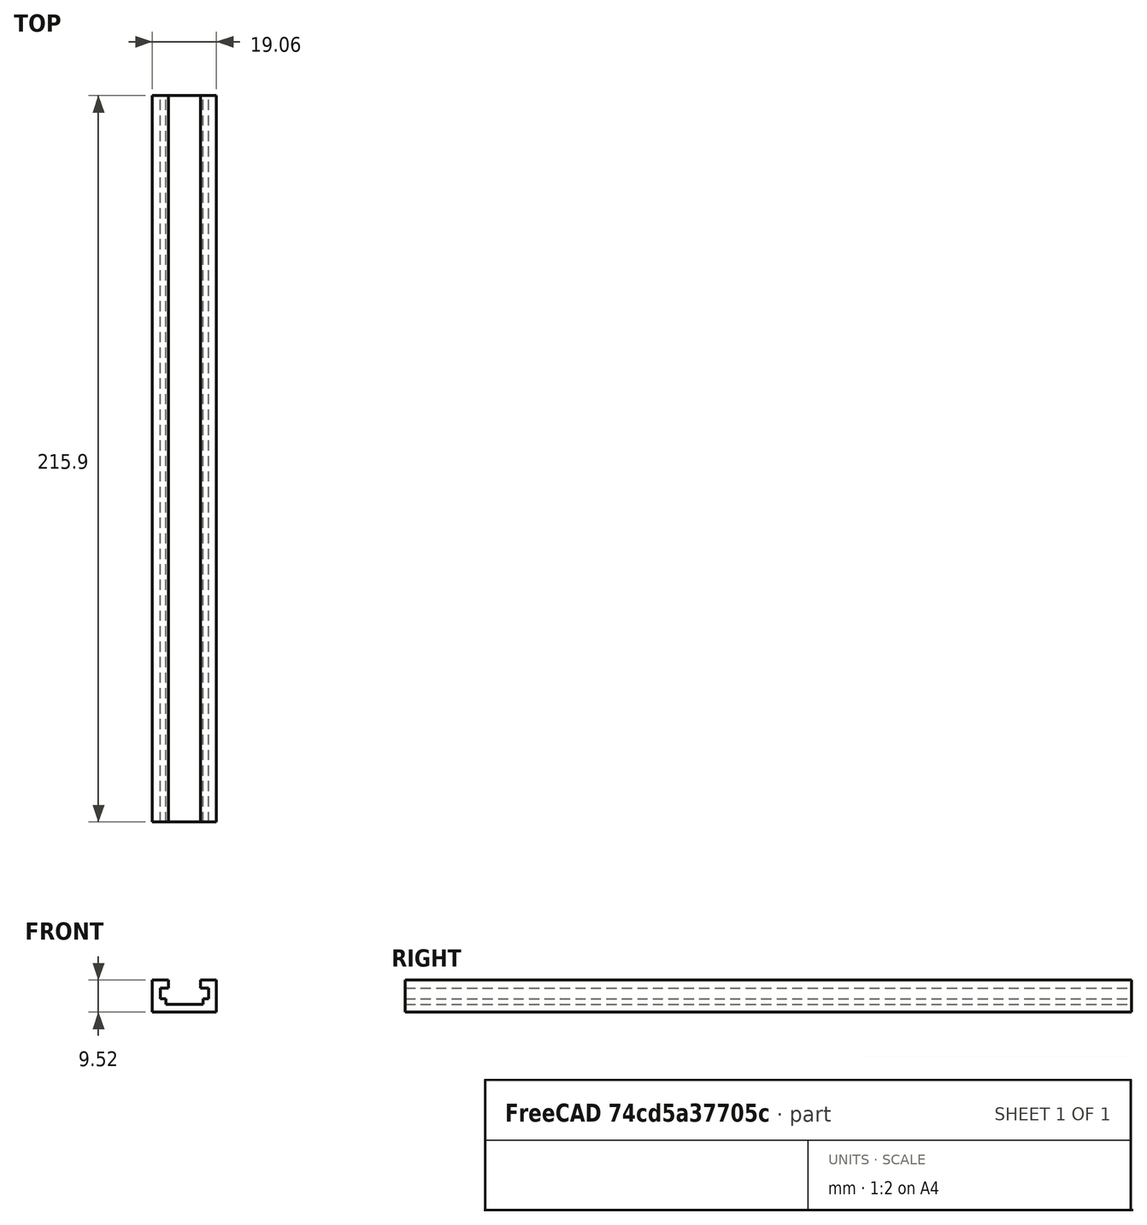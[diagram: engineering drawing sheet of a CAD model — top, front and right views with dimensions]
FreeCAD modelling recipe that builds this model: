
FCSTD DOCUMENT  (FreeCAD 0.20R29603 (Git))
Label: far_fence_top_t_track
License: All rights reserved
LicenseURL: http://en.wikipedia.org/wiki/All_rights_reserved
objects: Sketcher::SketchObject×4, PartDesign::Pocket×3, TechDraw::DrawProjGroupItem×2, PartDesign::Pad×1, PartDesign::Body×1, TechDraw::DrawSVGTemplate×1, TechDraw::DrawProjGroup×1, TechDraw::DrawViewDimension×1, TechDraw::DrawPage×1
note: 13 computed .brp shape members not serialized (recipe doc carries the construction recipe); baked Part::Feature solids carry a one-line shape summary decoded from their .brp

FEATURE [Sketcher::SketchObject] Sketch
  FullyConstrained = true
  MapMode = 5
  Placement = pos=(0,0,0) rot=(1,0,0;1.5708rad)
  Support = -> [XZ_Plane]
  sketch-geometry (5):
    g0: LineSegment StartX=-9.525 StartY=-4.7625 StartZ=0 EndX=-9.525 EndY=4.7625 EndZ=0
    g1: LineSegment StartX=-9.525 StartY=4.7625 StartZ=0 EndX=9.525 EndY=4.7625 EndZ=0
    g2: LineSegment StartX=9.525 StartY=4.7625 StartZ=0 EndX=9.525 EndY=-4.7625 EndZ=0
    g3: LineSegment StartX=9.525 StartY=-4.7625 StartZ=0 EndX=-9.525 EndY=-4.7625 EndZ=0
    g4: GeomPoint X=0 Y=0 Z=0
  constraints (12):
    c: Coincident(g0,g1)
    c: Coincident(g1,g2)
    c: Coincident(g2,g3)
    c: Coincident(g3,g0)
    c: Horizontal(g1)
    c: Horizontal(g3)
    c: Vertical(g0)
    c: Vertical(g2)
    c: Symmetric(g1,g0,g4)
    c: DistanceX(g1,g1) = 19.05
    c: DistanceY(g2,g2) = 9.525
    c: Coincident(g-1,g4)
FEATURE [PartDesign::Pad] Pad
  Direction = (0,-1,-2e-16)
  Length = 215.9
  Length2 = 10
  Placement = pos=(0,0,0) rot=(1,0,0;1.5708rad)
  Profile = -> Sketch
  ReferenceAxis = -> Sketch [N_Axis]
  Type = 0
FEATURE [Sketcher::SketchObject] Sketch001
  ExternalGeometry = -> [Pad]
  FullyConstrained = true
  MapMode = 5
  Placement = pos=(0,-215.9,-4.75e-14) rot=(1,0,0;1.5708rad)
  Support = -> [Pad]
  sketch-geometry (5):
    g0: LineSegment StartX=-4.7625 StartY=2.38125 StartZ=0 EndX=-4.7625 EndY=4.7625 EndZ=0
    g1: LineSegment StartX=-4.7625 StartY=4.7625 StartZ=0 EndX=4.7625 EndY=4.7625 EndZ=0
    g2: LineSegment StartX=4.7625 StartY=4.7625 StartZ=0 EndX=4.7625 EndY=2.38125 EndZ=0
    g3: LineSegment StartX=4.7625 StartY=2.38125 StartZ=0 EndX=-4.7625 EndY=2.38125 EndZ=0
    g4: GeomPoint X=0 Y=3.57187 Z=0
  constraints (12):
    c: Coincident(g0,g1)
    c: Coincident(g1,g2)
    c: Coincident(g2,g3)
    c: Coincident(g3,g0)
    c: Horizontal(g3)
    c: Vertical(g0)
    c: Vertical(g2)
    c: Symmetric(g1,g0,g4)
    c: Tangent(g1,g-3)
    c: DistanceX(g3,g3) = 9.525
    c: Distance(g2,g-4) = 7.14375
    c: PointOnObject(g4,g-2)
FEATURE [PartDesign::Pocket] Pocket
  BaseFeature = -> Pad
  Direction = (0,1,2e-16)
  Length = 5
  Length2 = 5
  Placement = pos=(0,0,0) rot=(1,0,0;1.5708rad)
  Profile = -> Sketch001
  ReferenceAxis = -> Sketch001 [N_Axis]
  Type = 1
FEATURE [Sketcher::SketchObject] Sketch002
  ExternalGeometry = -> [Pocket]
  FullyConstrained = true
  MapMode = 5
  Placement = pos=(0,-215.9,-4.75e-14) rot=(1,0,0;1.5708rad)
  Support = -> [Pocket]
  sketch-geometry (5):
    g0: LineSegment StartX=-7.14375 StartY=2.38125 StartZ=0 EndX=-7.14375 EndY=-0.79375 EndZ=0
    g1: LineSegment StartX=-7.14375 StartY=-0.79375 StartZ=0 EndX=7.14375 EndY=-0.79375 EndZ=0
    g2: LineSegment StartX=7.14375 StartY=-0.79375 StartZ=0 EndX=7.14375 EndY=2.38125 EndZ=0
    g3: LineSegment StartX=7.14375 StartY=2.38125 StartZ=0 EndX=-7.14375 EndY=2.38125 EndZ=0
    g4: GeomPoint X=0 Y=0.79375 Z=0
  constraints (12):
    c: Coincident(g0,g1)
    c: Coincident(g1,g2)
    c: Coincident(g2,g3)
    c: Coincident(g3,g0)
    c: Horizontal(g1)
    c: Vertical(g0)
    c: Vertical(g2)
    c: Symmetric(g1,g0,g4)
    c: Tangent(g3,g-3)
    c: PointOnObject(g4,g-2)
    c: Distance(g0,g-4) = 3.96875
    c: DistanceX(g1,g1) = 14.2875
FEATURE [PartDesign::Pocket] Pocket001
  BaseFeature = -> Pocket
  Direction = (0,1,2e-16)
  Length = 5
  Length2 = 5
  Placement = pos=(0,0,0) rot=(1,0,0;1.5708rad)
  Profile = -> Sketch002
  ReferenceAxis = -> Sketch002 [N_Axis]
  Type = 1
FEATURE [Sketcher::SketchObject] Sketch003
  ExternalGeometry = -> [Pocket001]
  FullyConstrained = true
  MapMode = 5
  Placement = pos=(0,-215.9,-4.75e-14) rot=(1,0,0;1.5708rad)
  Support = -> [Pocket001]
  sketch-geometry (5):
    g0: LineSegment StartX=-5.55625 StartY=-0.79375 StartZ=0 EndX=-5.55625 EndY=-2.38125 EndZ=0
    g1: LineSegment StartX=-5.55625 StartY=-2.38125 StartZ=0 EndX=5.55625 EndY=-2.38125 EndZ=0
    g2: LineSegment StartX=5.55625 StartY=-2.38125 StartZ=0 EndX=5.55625 EndY=-0.79375 EndZ=0
    g3: LineSegment StartX=5.55625 StartY=-0.79375 StartZ=0 EndX=-5.55625 EndY=-0.79375 EndZ=0
    g4: GeomPoint X=0 Y=-1.5875 Z=0
  constraints (12):
    c: Coincident(g0,g1)
    c: Coincident(g1,g2)
    c: Coincident(g2,g3)
    c: Coincident(g3,g0)
    c: Horizontal(g1)
    c: Vertical(g0)
    c: Vertical(g2)
    c: Symmetric(g1,g0,g4)
    c: DistanceX(g1,g1) = 11.1125
    c: PointOnObject(g4,g-2)
    c: DistanceY(g0,g0) = 1.5875
    c: Tangent(g-3,g3)
FEATURE [PartDesign::Pocket] Pocket002
  BaseFeature = -> Pocket001
  Direction = (0,1,2e-16)
  Length = 5
  Length2 = 5
  Placement = pos=(0,0,0) rot=(1,0,0;1.5708rad)
  Profile = -> Sketch003
  ReferenceAxis = -> Sketch003 [N_Axis]
  Type = 1
FEATURE [PartDesign::Body] Body
  Group = -> [Sketch,Pad,Sketch001,Pocket,Sketch002,Pocket001,Sketch003,Pocket002]
  Origin = -> Origin
  Tip = -> Pocket002
FEATURE [TechDraw::DrawSVGTemplate] Template
  Height = 297
  Orientation = 1
  Width = 420
FEATURE [TechDraw::DrawProjGroupItem] ProjItem  label="Front"
  CoarseView = false
  Direction = (0,-4e-16,1)
  Focus = 100
  HardHidden = false
  IsoCount = 0
  IsoHidden = false
  IsoVisible = false
  LockPosition = true
  Perspective = false
  Rotation = 0
  RotationVector = (0,1,0)
  ScaleType = 2
  SeamHidden = false
  SeamVisible = true
  SmoothHidden = false
  SmoothVisible = true
  Source = -> [Body]
  Type = 0
  X = 0
  XDirection = (0,1,4e-16)
  Y = 0
FEATURE [TechDraw::DrawProjGroupItem] ProjItem001  label="FrontTopRight"
  CoarseView = false
  Direction = (-0.57735,0.57735,0.57735)
  Focus = 100
  HardHidden = false
  IsoCount = 0
  IsoHidden = false
  IsoVisible = false
  LockPosition = false
  Perspective = false
  Rotation = 0
  RotationVector = (1,0,0)
  ScaleType = 2
  SeamHidden = false
  SeamVisible = true
  SmoothHidden = false
  SmoothVisible = true
  Source = -> [Body]
  Type = 7
  X = 124.521
  XDirection = (0,0.707107,-0.707107)
  Y = 80.9857
FEATURE [TechDraw::DrawProjGroup] ProjGroup
  Anchor = -> ProjItem
  AutoDistribute = false
  LockPosition = false
  ProjectionType = 1
  Rotation = 0
  ScaleType = 0
  Source = -> [Body]
  Views = -> [ProjItem,ProjItem001]
  X = 198.603
  Y = 142.408
  spacingX = 15.0812
  spacingY = 15.0812
FEATURE [TechDraw::DrawViewDimension] Dimension
  AngleOverride = false
  Arbitrary = false
  ArbitraryTolerances = false
  EqualTolerance = true
  ExtensionAngle = 0
  FormatSpec = %.2w
  FormatSpecOverTolerance = %+.2w
  FormatSpecUnderTolerance = %+.2w
  Inverted = false
  LineAngle = 0
  LockPosition = false
  MeasureType = 1
  OverTolerance = 0
  References2D = -> [ProjItem]
  Rotation = 0
  ScaleType = 0
  TheoreticalExact = false
  Type = 1
  UnderTolerance = 0
  X = 0
  Y = -6.94531
FEATURE [TechDraw::DrawPage] Page
  KeepUpdated = true
  NextBalloonIndex = 1
  ProjectionType = 0
  Template = -> Template
  Views = -> [ProjGroup,Dimension]
